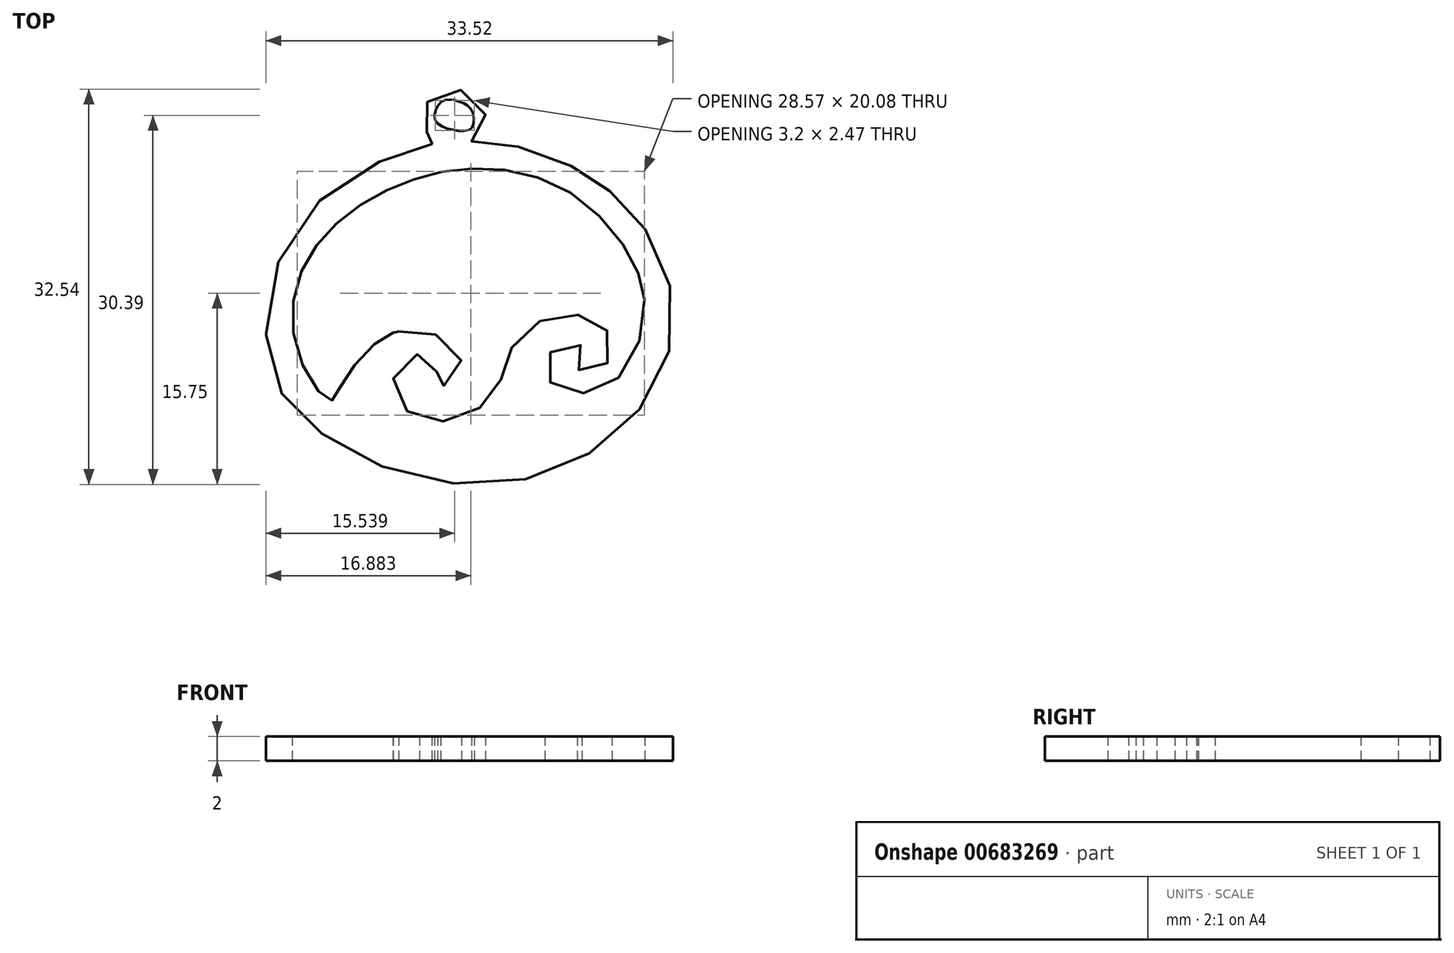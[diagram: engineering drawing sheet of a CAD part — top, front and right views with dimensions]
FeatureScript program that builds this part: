
annotation { "Feature Type Name" : "Feature", "Feature Type Description" : "" }
export const myFeature = defineFeature(function(context is Context, id is Id, definition is map)
    precondition{}
    {
        {
            var Q0;
            Q0=qCreatedBy(makeId("Top.planeOp"),FACE);
            var sketch = newSketch(context, id + "F0", { "sketchPlane" : qUnion([Q0])});
            skFitSpline(sketch, "E0", {"points": [v(-48.77, 50.24) * mm, v(-48.08, 50.7) * mm, v(-49.55, 51.48) * mm, v(-49.4, 53.42) * mm, v(-47.3, 54.73) * mm, v(-45.06, 53.96) * mm, v(-44.52, 51.8) * mm, v(-45.53, 50.48) * mm, v(-41.66, 50.01) * mm, v(-36.47, 47.92) * mm, v(-33.38, 45.68) * mm, v(-29.9, 40.8) * mm, v(-29.28, 33.15) * mm, v(-33.53, 26.5) * mm, v(-41.12, 22.63) * mm, v(-50.86, 23.01) * mm, v(-58.6, 26.96) * mm, v(-62, 31.6) * mm, v(-61.38, 40.65) * mm, v(-54.89, 47.92) * mm, v(-48.77, 50.24) * mm]});
            skFitSpline(sketch, "E1", {"points": [v(-57.13, 29.12) * mm, v(-59.68, 32.68) * mm, v(-59.68, 39.41) * mm, v(-56.05, 44.2) * mm, v(-50.79, 47.15) * mm, v(-44.9, 48.23) * mm, v(-37.25, 46.14) * mm, v(-31.83, 39.65) * mm, v(-31.45, 35.16) * mm, v(-33.46, 30.98) * mm, v(-36.94, 29.74) * mm, v(-39.34, 31.06) * mm, v(-38.64, 33.46) * mm, v(-36.47, 33.53) * mm, v(-36.78, 31.75) * mm, v(-34.7, 31.83) * mm, v(-34.15, 34.46) * mm, v(-36.24, 36.09) * mm, v(-39.96, 35.62) * mm, v(-42.5, 32.91) * mm, v(-43.36, 30.2) * mm, v(-45.99, 27.89) * mm, v(-49.7, 27.65) * mm, v(-51.95, 29.98) * mm, v(-50.63, 32.84) * mm, v(-48.31, 31.99) * mm, v(-48.77, 30.67) * mm, v(-47, 30.6) * mm, v(-46.76, 33.46) * mm, v(-50.32, 34.85) * mm, v(-52.95, 34.23) * mm, v(-56.28, 30.36) * mm, v(-57.13, 29.12) * mm]});
            skFitSpline(sketch, "E2", {"points": [v(-59.68, 35.62) * mm, v(-58.21, 37.25) * mm, v(-56.12, 38.87) * mm, v(-53.42, 39.5) * mm, v(-51.56, 38.25) * mm, v(-53.1, 37.87) * mm, v(-54.19, 35.85) * mm, v(-51.97, 34.71) * mm, v(-50.01, 36.24) * mm, v(-48.54, 38.72) * mm, v(-46.53, 40.03) * mm, v(-44.67, 40.42) * mm, v(-42.74, 39.41) * mm, v(-44.21, 38.87) * mm, v(-45.53, 37.32) * mm, v(-44.21, 36.24) * mm, v(-41.66, 36.32) * mm, v(-39.96, 38.1) * mm, v(-39.26, 40.42) * mm, v(-36.16, 41.5) * mm, v(-33.92, 40.8) * mm, v(-33.77, 40.5) * mm, v(-35.62, 40.03) * mm, v(-35.93, 38.33) * mm, v(-34.46, 37.32) * mm, v(-31.3, 37.45) * mm], "startDerivative": vector(34.37, 40.7) * mm, "endDerivative": vector(70.15, 9.34) * mm});
            skFitSpline(sketch, "E3", {"points": [v(-47.07, 51.4) * mm, v(-48.54, 52.25) * mm, v(-48, 53.72) * mm, v(-46.76, 53.8) * mm, v(-45.53, 53.03) * mm, v(-45.53, 51.56) * mm, v(-47.07, 51.4) * mm]});
            skSolve(sketch);
        }
        {
            var Q0;
            Q0 = qSketchRegion(id + "F0", true);
            extrude(context, id + "F1", {"entities" : qUnion([Q0]), "depth" : 2 * mm, "offsetDistance" : 25 * mm});
        }
    });
